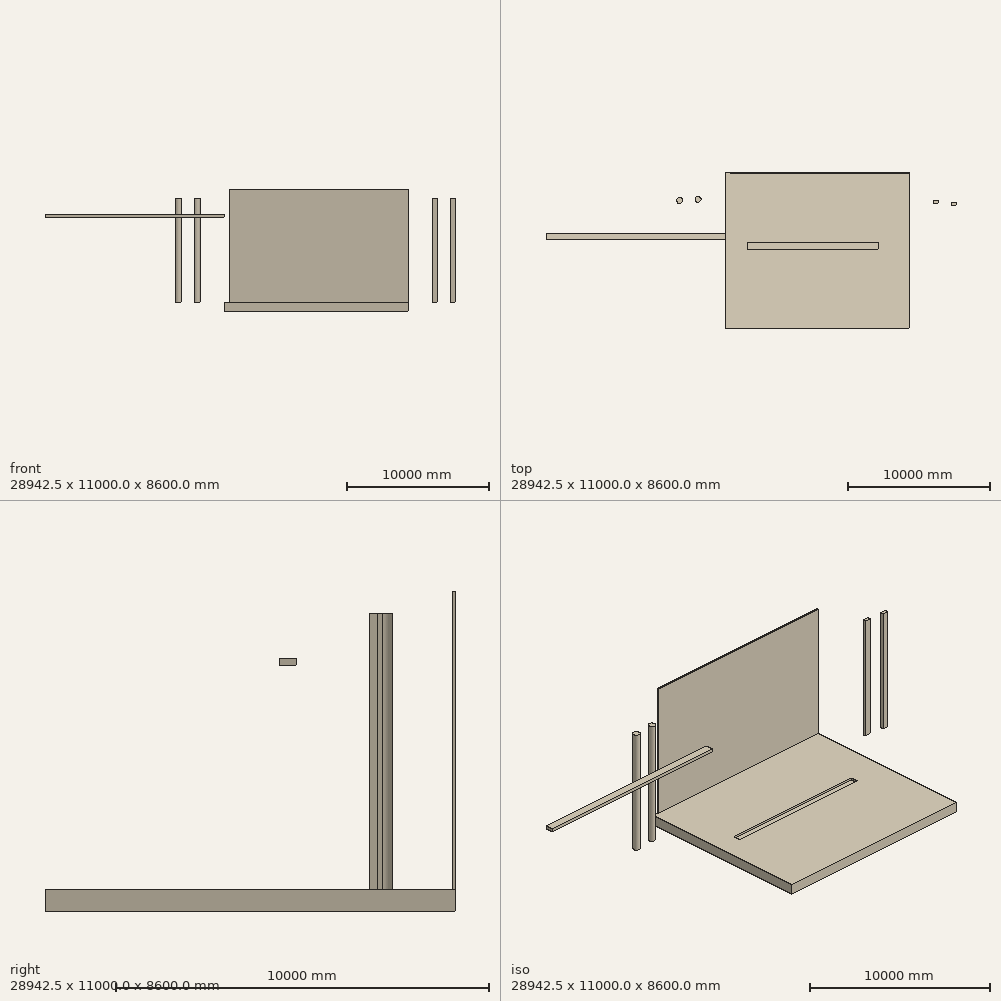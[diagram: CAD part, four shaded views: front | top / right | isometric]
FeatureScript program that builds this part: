
annotation { "Feature Type Name" : "Feature", "Feature Type Description" : "" }
export const myFeature = defineFeature(function(context is Context, id is Id, definition is map)
    precondition{}
    {
        {
            var Q0;
            Q0=qCreatedBy(makeId("Top.planeOp"),FACE);
            var sketch = newSketch(context, id + "F0", { "sketchPlane" : qUnion([Q0])});
            skLineSegment(sketch, "E0.bottom", {"start": v(6500, -5500) * mm, "end": v(-6500, -5500) * mm});
            skLineSegment(sketch, "E0.top", {"start": v(6500, 5500) * mm, "end": v(-6500, 5500) * mm});
            skLineSegment(sketch, "E0.left", {"start": v(6500, -5500) * mm, "end": v(6500, 5500) * mm});
            skLineSegment(sketch, "E0.right", {"start": v(-6500, -5500) * mm, "end": v(-6500, 5500) * mm});
            skPoint(sketch, "E0.middle", {"position": v(0, 0) * mm});
            skSolve(sketch);
        }
        {
            var Q0;
            Q0=makeQuery(id+"F0.imprint","IMPRINT",FACE,{"disambiguationData":[TD([[makeQuery(id+"F0.imprint","IMPRINT",EDGE,{"derivedFrom":sQuery(id+"F0.wireOp",EDGE,"E0.bottom")}),-1.0]])]});
            extrude(context, id + "F1", {"entities" : qUnion([Q0]), "depth" : 600 * mm, "offsetDistance" : 25 * mm});
        }
        {
            var Q0;
            Q0=makeQuery(id+"F1.opExtrude","CAP_FACE",FACE,{"disambiguationData":[OSD([sQuery(id+"F0.wireOp",EDGE,"E0.bottom"),sQuery(id+"F0.wireOp",EDGE,"E0.top"),sQuery(id+"F0.wireOp",EDGE,"E0.left"),sQuery(id+"F0.wireOp",EDGE,"E0.right")])],"isStart":false});
            var sketch = newSketch(context, id + "F2", { "sketchPlane" : qUnion([Q0])});
            skLineSegment(sketch, "E1.bottom", {"start": v(-6155.03, 5411.76) * mm, "end": v(6844.97, 5411.76) * mm});
            skLineSegment(sketch, "E1.top", {"start": v(-6155.03, 5711.76) * mm, "end": v(6844.97, 5711.76) * mm});
            skLineSegment(sketch, "E1.left", {"start": v(-6155.03, 5411.76) * mm, "end": v(-6155.03, 5711.76) * mm});
            skLineSegment(sketch, "E1.right", {"start": v(6844.97, 5411.76) * mm, "end": v(6844.97, 5711.76) * mm});
            skSolve(sketch);
        }
        {
            var Q0;
            Q0=makeQuery(id+"F2.imprint","IMPRINT",FACE,{"disambiguationData":[TD([[makeQuery(id+"F2.imprint","IMPRINT",EDGE,{"derivedFrom":sQuery(id+"F2.wireOp",EDGE,"E1.bottom")}),1.0]])]});
            extrude(context, id + "F3", {"entities" : qUnion([Q0]), "depth" : 8000 * mm, "offsetDistance" : 25 * mm});
        }
        {
            var Q0;
            Q0=makeQuery(id+"F1.opExtrude","CAP_FACE",FACE,{"disambiguationData":[OSD([sQuery(id+"F0.wireOp",EDGE,"E0.bottom"),sQuery(id+"F0.wireOp",EDGE,"E0.top"),sQuery(id+"F0.wireOp",EDGE,"E0.left"),sQuery(id+"F0.wireOp",EDGE,"E0.right")])],"isStart":false});
            var sketch = newSketch(context, id + "F4", { "sketchPlane" : qUnion([Q0])});
            skLineSegment(sketch, "E2.bottom", {"start": v(8173.5, 3544.96) * mm, "end": v(8523.5, 3544.96) * mm});
            skLineSegment(sketch, "E2.top", {"start": v(8173.5, 3344.96) * mm, "end": v(8523.5, 3344.96) * mm});
            skLineSegment(sketch, "E2.left", {"start": v(8173.5, 3544.96) * mm, "end": v(8173.5, 3344.96) * mm});
            skLineSegment(sketch, "E2.right", {"start": v(8523.5, 3544.96) * mm, "end": v(8523.5, 3344.96) * mm});
            skLineSegment(sketch, "E3.bottom", {"start": v(9437.46, 3403.31) * mm, "end": v(9787.46, 3403.31) * mm});
            skLineSegment(sketch, "E3.top", {"start": v(9437.46, 3203.31) * mm, "end": v(9787.46, 3203.31) * mm});
            skLineSegment(sketch, "E3.left", {"start": v(9437.46, 3403.31) * mm, "end": v(9437.46, 3203.31) * mm});
            skLineSegment(sketch, "E3.right", {"start": v(9787.46, 3403.31) * mm, "end": v(9787.46, 3203.31) * mm});
            skSolve(sketch);
        }
        {
            var Q0;
            Q0=makeQuery(id+"F4.imprint","IMPRINT",FACE,{"disambiguationData":[TD([[makeQuery(id+"F4.imprint","IMPRINT",EDGE,{"derivedFrom":sQuery(id+"F4.wireOp",EDGE,"E2.bottom")}),-1.0]])]});
            var Q1;
            Q1=makeQuery(id+"F4.imprint","IMPRINT",FACE,{"disambiguationData":[TD([[makeQuery(id+"F4.imprint","IMPRINT",EDGE,{"derivedFrom":sQuery(id+"F4.wireOp",EDGE,"E3.bottom")}),-1.0]])]});
            extrude(context, id + "F5", {"entities" : qUnion([Q0, Q1]), "depth" : 7400 * mm, "offsetDistance" : 25 * mm});
        }
        {
            var Q0;
            Q0=makeQuery(id+"F1.opExtrude","CAP_FACE",FACE,{"disambiguationData":[OSD([sQuery(id+"F0.wireOp",EDGE,"E0.bottom"),sQuery(id+"F0.wireOp",EDGE,"E0.top"),sQuery(id+"F0.wireOp",EDGE,"E0.left"),sQuery(id+"F0.wireOp",EDGE,"E0.right")])],"isStart":false});
            var sketch = newSketch(context, id + "F6", { "sketchPlane" : qUnion([Q0])});
            skLineSegment(sketch, "E4.bottom", {"start": v(-5000, 600) * mm, "end": v(4300, 600) * mm});
            skLineSegment(sketch, "E4.top", {"start": v(-5000, 100) * mm, "end": v(4300, 100) * mm});
            skLineSegment(sketch, "E4.left", {"start": v(-5000, 600) * mm, "end": v(-5000, 100) * mm});
            skLineSegment(sketch, "E4.right", {"start": v(4300, 600) * mm, "end": v(4300, 100) * mm});
            skSolve(sketch);
        }
        {
            var Q0;
            Q0 = qSketchRegion(id + "F6", true);
            extrude(context, id + "F7", {"entities" : qUnion([Q0]), "operationType" : NewBodyOperationType.REMOVE, "oppositeDirection" : true, "depth" : 150 * mm, "offsetDistance" : 25 * mm});
        }
        {
            var Q0;
            Q0=makeQuery(id+"F1.opExtrude","CAP_FACE",FACE,{"disambiguationData":[OSD([sQuery(id+"F0.wireOp",EDGE,"E0.bottom"),sQuery(id+"F0.wireOp",EDGE,"E0.top"),sQuery(id+"F0.wireOp",EDGE,"E0.left"),sQuery(id+"F0.wireOp",EDGE,"E0.right")])],"isStart":false});
            var sketch = newSketch(context, id + "F8", { "sketchPlane" : qUnion([Q0])});
            skCircle(sketch, "E5", {"center": v(-9750.67, 3522.12) * mm, "radius": 210 * mm});
            skCircle(sketch, "E6", {"center": v(-8452.21, 3597.39) * mm, "radius": 210 * mm});
            skSolve(sketch);
        }
        {
            var Q0;
            Q0=makeQuery(id+"F8.imprint","IMPRINT",FACE,{"disambiguationData":[TD([[makeQuery(id+"F8.imprint","IMPRINT",EDGE,{"derivedFrom":sQuery(id+"F8.wireOp",EDGE,"E5")}),1.0]])]});
            var Q1;
            Q1=makeQuery(id+"F8.imprint","IMPRINT",FACE,{"disambiguationData":[TD([[makeQuery(id+"F8.imprint","IMPRINT",EDGE,{"derivedFrom":sQuery(id+"F8.wireOp",EDGE,"E6")}),1.0]])]});
            extrude(context, id + "F9", {"entities" : qUnion([Q0, Q1]), "depth" : 7400 * mm, "offsetDistance" : 25 * mm});
        }
        {
            var Q0;
            Q0=makeQuery(id+"F1.opExtrude","SWEPT_FACE",FACE,{"disambiguationData":[OSD([sQuery(id+"F0.wireOp",EDGE,"E0.right")])]});
            var sketch = newSketch(context, id + "F10", { "sketchPlane" : qUnion([Q0])});
            skLineSegment(sketch, "E7.bottom", {"start": v(-1233.04, 6807.9) * mm, "end": v(-783.04, 6807.9) * mm});
            skLineSegment(sketch, "E7.top", {"start": v(-1233.04, 6607.9) * mm, "end": v(-783.04, 6607.9) * mm});
            skLineSegment(sketch, "E7.left", {"start": v(-1233.04, 6807.9) * mm, "end": v(-1233.04, 6607.9) * mm});
            skLineSegment(sketch, "E7.right", {"start": v(-783.04, 6807.9) * mm, "end": v(-783.04, 6607.9) * mm});
            skSolve(sketch);
        }
        {
            var Q0;
            Q0=makeQuery(id+"F10.imprint","IMPRINT",FACE,{"disambiguationData":[TD([[makeQuery(id+"F10.imprint","IMPRINT",EDGE,{"derivedFrom":sQuery(id+"F10.wireOp",EDGE,"E7.bottom")}),-1.0]])]});
            extrude(context, id + "F11", {"entities" : qUnion([Q0]), "depth" : 12655 * mm, "offsetDistance" : 25 * mm});
        }
    });
